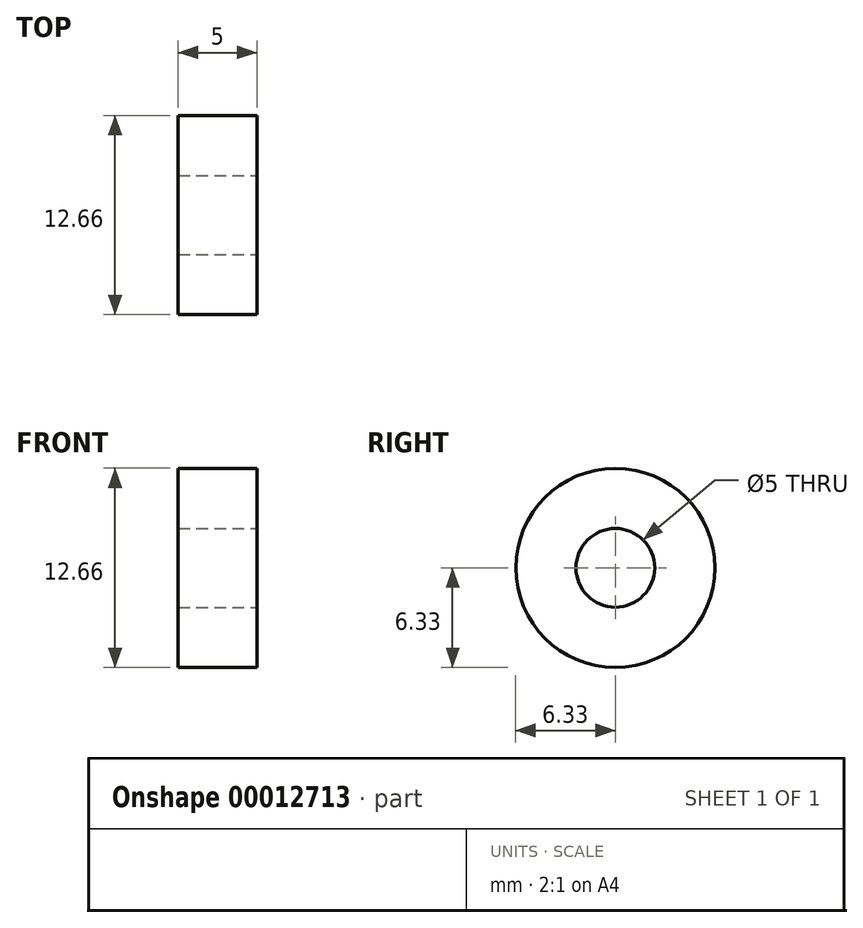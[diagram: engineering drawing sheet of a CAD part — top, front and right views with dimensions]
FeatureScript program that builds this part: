
annotation { "Feature Type Name" : "Feature", "Feature Type Description" : "" }
export const myFeature = defineFeature(function(context is Context, id is Id, definition is map)
    precondition{}
    {
        {
            var Q0;
            Q0=qCreatedBy(makeId("Right.planeOp"),FACE);
            var sketch = newSketch(context, id + "F0", { "sketchPlane" : qUnion([Q0])});
            skCircle(sketch, "E0", {"center": v(0, 0) * mm, "radius": 6.33 * mm});
            skCircle(sketch, "E1", {"center": v(0, 0) * mm, "radius": 2.5 * mm});
            skSolve(sketch);
        }
        {
            var Q0;
            Q0=makeQuery(id+"F0.imprint","IMPRINT",FACE,{"disambiguationData":[TD([[makeQuery(id+"F0.imprint","IMPRINT",EDGE,{"derivedFrom":sQuery(id+"F0.wireOp",EDGE,"E0")}),1.0]])]});
            extrude(context, id + "F1", {"entities" : qUnion([Q0]), "oppositeDirection" : true, "depth" : 5 * mm});
        }
    });
